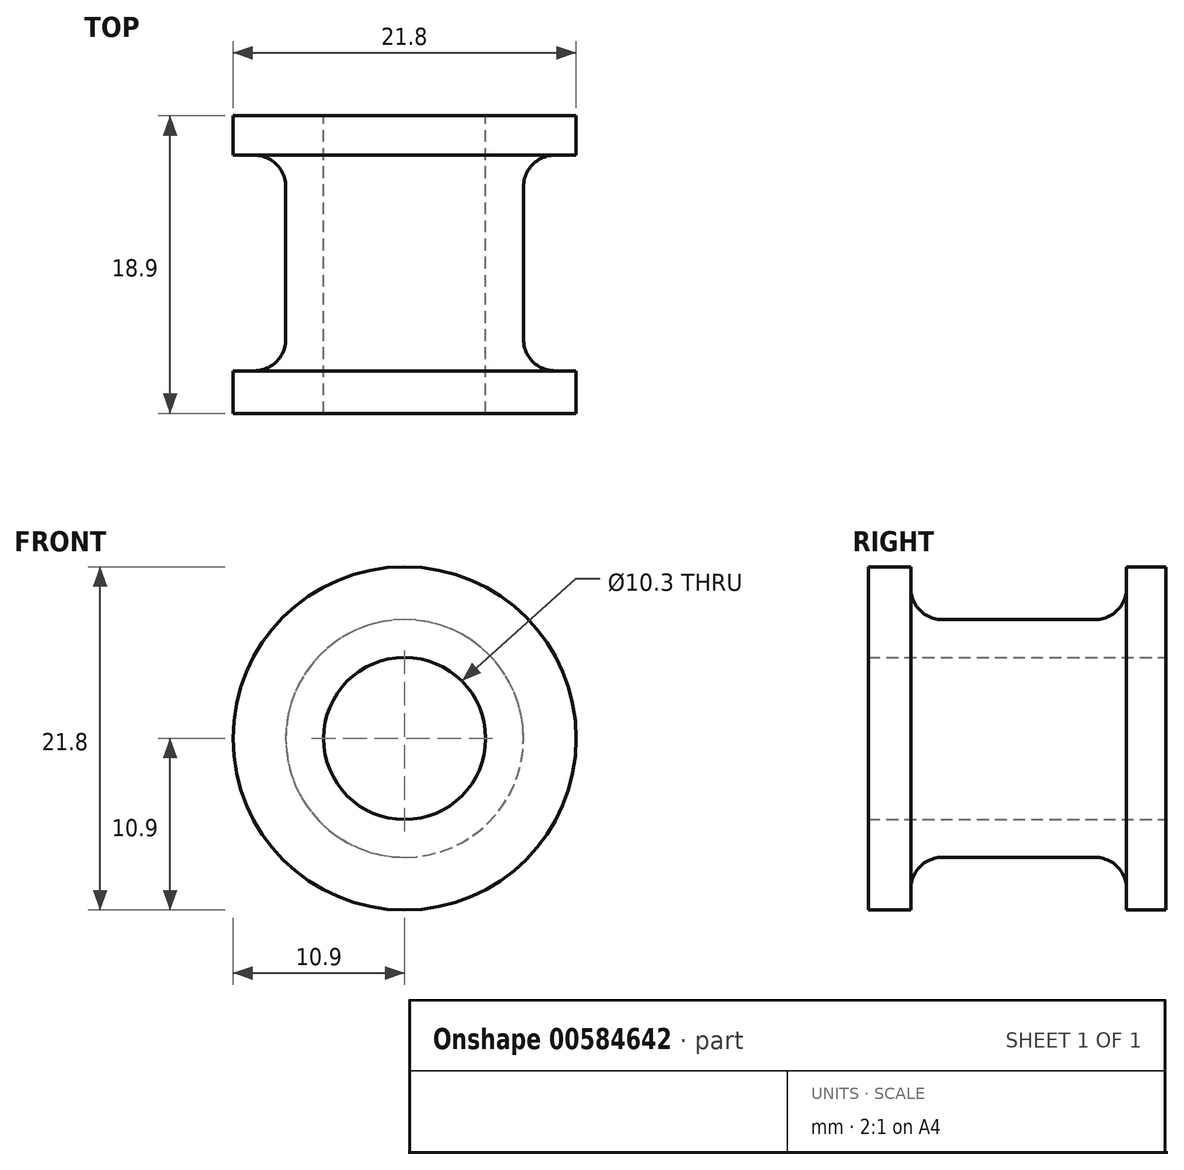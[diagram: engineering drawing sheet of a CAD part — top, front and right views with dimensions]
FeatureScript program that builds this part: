
annotation { "Feature Type Name" : "Feature", "Feature Type Description" : "" }
export const myFeature = defineFeature(function(context is Context, id is Id, definition is map)
    precondition{}
    {
        {
            var Q0;
            Q0=qCreatedBy(makeId("Front.planeOp"),FACE);
            var sketch = newSketch(context, id + "F0", { "sketchPlane" : qUnion([Q0])});
            skCircle(sketch, "E0", {"center": v(0, 0) * mm, "radius": 7.55 * mm});
            skSolve(sketch);
        }
        {
            var Q0;
            Q0=makeQuery(id+"F0.imprint","IMPRINT",FACE,{"disambiguationData":[TD([[makeQuery(id+"F0.imprint","IMPRINT",EDGE,{"derivedFrom":sQuery(id+"F0.wireOp",EDGE,"E0")}),1.0]])]});
            extrude(context, id + "F1", {"entities" : qUnion([Q0]), "depth" : 18.7 * mm, "offsetDistance" : 25 * mm});
        }
        {
            var Q0;
            Q0=makeQuery(id+"F1.opExtrude","CAP_FACE",FACE,{"disambiguationData":[OSD([sQuery(id+"F0.wireOp",EDGE,"E0")])],"isStart":true});
            var sketch = newSketch(context, id + "F2", { "sketchPlane" : qUnion([Q0])});
            skCircle(sketch, "E1", {"center": v(0, 0) * mm, "radius": 10.9 * mm});
            skSolve(sketch);
        }
        {
            var Q0;
            Q0 = qSketchRegion(id + "F2", true);
            extrude(context, id + "F3", {"entities" : qUnion([Q0]), "operationType" : NewBodyOperationType.ADD, "oppositeDirection" : true, "depth" : 2.3 * mm, "offsetDistance" : 25 * mm});
        }
        {
            var Q0;
            Q0 = qSketchRegion(id + "F2", true);
            extrude(context, id + "F4", {"entities" : qUnion([Q0]), "operationType" : NewBodyOperationType.ADD, "depth" : 0.2 * mm, "offsetDistance" : 25 * mm});
        }
        {
            var Q0;
            Q0=makeQuery(id+"F1.opExtrude","CAP_FACE",FACE,{"disambiguationData":[OSD([sQuery(id+"F0.wireOp",EDGE,"E0")])],"isStart":false});
            var sketch = newSketch(context, id + "F5", { "sketchPlane" : qUnion([Q0])});
            skCircle(sketch, "E2", {"center": v(0, 0) * mm, "radius": 10.9 * mm});
            skSolve(sketch);
        }
        {
            var Q0;
            Q0 = qSketchRegion(id + "F5", true);
            extrude(context, id + "F6", {"entities" : qUnion([Q0]), "operationType" : NewBodyOperationType.ADD, "oppositeDirection" : true, "depth" : 2.7 * mm, "offsetDistance" : 25 * mm});
        }
        {
            var Q0;
            Q0=qCreatedBy(makeId("Front.planeOp"),FACE);
            var sketch = newSketch(context, id + "F7", { "sketchPlane" : qUnion([Q0])});
            skCircle(sketch, "E3", {"center": v(0, 0) * mm, "radius": 5.15 * mm});
            skSolve(sketch);
        }
        {
            var Q0;
            Q0 = qSketchRegion(id + "F7", true);
            extrude(context, id + "F8", {"entities" : qUnion([Q0]), "operationType" : NewBodyOperationType.REMOVE, "endBound" : BoundingType.SYMMETRIC, "depth" : 100 * mm, "offsetDistance" : 25 * mm});
        }
        {
            var Q0;
            Q0=makeQuery(id+"F3.boolean.opBoolean","INTERSECT",EDGE,{"derivedFrom":[makeQuery(id+"F1.opExtrude","SWEPT_FACE",FACE,{"disambiguationData":[OSD([sQuery(id+"F0.wireOp",EDGE,"E0")])]}),makeQuery(id+"F3.opExtrude","CAP_FACE",FACE,{"disambiguationData":[OSD([sQuery(id+"F2.wireOp",EDGE,"E1")])],"isStart":false})]});
            var Q1;
            Q1=makeQuery(id+"F6.boolean.opBoolean","INTERSECT",EDGE,{"derivedFrom":[makeQuery(id+"F1.opExtrude","SWEPT_FACE",FACE,{"disambiguationData":[OSD([sQuery(id+"F0.wireOp",EDGE,"E0")])]}),makeQuery(id+"F6.opExtrude","CAP_FACE",FACE,{"disambiguationData":[OSD([sQuery(id+"F5.wireOp",EDGE,"E2")])],"isStart":false})]});
            fillet(context, id + "F9", {"entities" : qUnion([Q0, Q1]), "radius" : 2 * mm, "tangentPropagation" : true, "allowEdgeOverflow" : false});
        }
    });
